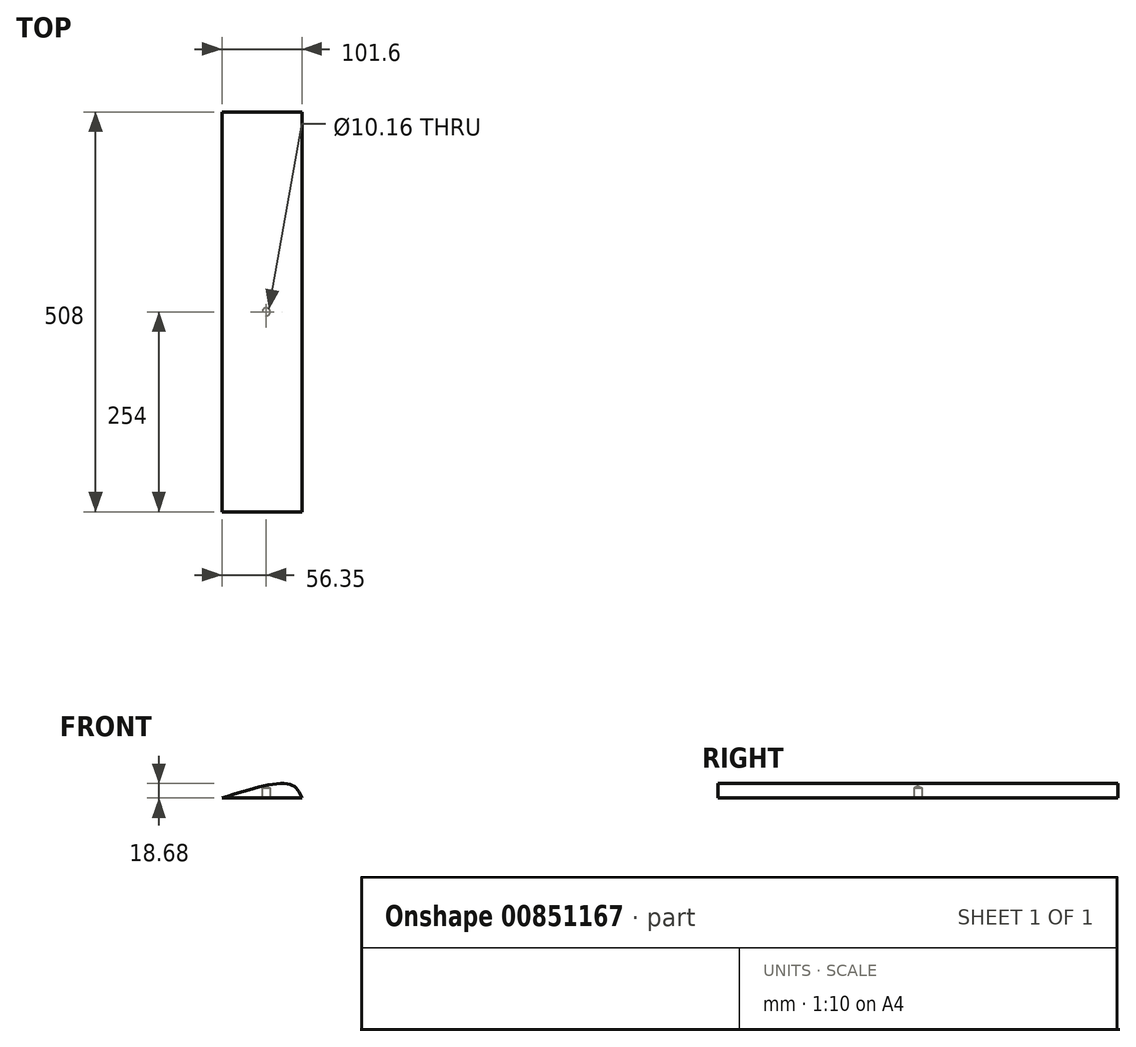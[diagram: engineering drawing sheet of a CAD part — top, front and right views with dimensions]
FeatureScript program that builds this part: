
annotation { "Feature Type Name" : "Feature", "Feature Type Description" : "" }
export const myFeature = defineFeature(function(context is Context, id is Id, definition is map)
    precondition{}
    {
        {
            var Q0;
            Q0=qCreatedBy(makeId("Front.planeOp"),FACE);
            var sketch = newSketch(context, id + "F0", { "sketchPlane" : qUnion([Q0])});
            skLineSegment(sketch, "E0", {"start": v(-56.35, 0) * mm, "end": v(45.25, 0) * mm});
            skFitSpline(sketch, "E1", {"points": [v(45.25, 0) * mm, v(31.12, 17.16) * mm, v(-56.35, 0) * mm], "startDerivative": vector(-27.65, 64.38) * mm, "endDerivative": vector(-160.74, -51.48) * mm});
            skSolve(sketch);
        }
        {
            var Q0;
            Q0=makeQuery(id+"F0.imprint","IMPRINT",FACE,{"disambiguationData":[TD([[makeQuery(id+"F0.imprint","IMPRINT",EDGE,{"derivedFrom":sQuery(id+"F0.wireOp",EDGE,"E0")}),1.0]])]});
            extrude(context, id + "F1", {"entities" : qUnion([Q0]), "endBound" : BoundingType.SYMMETRIC, "depth" : 508 * mm, "offsetDistance" : 25.4 * mm});
        }
        {
            var Q0;
            Q0=makeQuery(id+"F1.opExtrude","SWEPT_FACE",FACE,{"disambiguationData":[OSD([sQuery(id+"F0.wireOp",EDGE,"E0")])]});
            var sketch = newSketch(context, id + "F2", { "sketchPlane" : qUnion([Q0])});
            skCircle(sketch, "E2", {"center": v(0, 0) * mm, "radius": 5.08 * mm});
            skSolve(sketch);
        }
        {
            var Q0;
            Q0=sQuery(id+"F2.wireOp",VERTEX,"E2.center");
            var Q1;
            Q1=makeQuery(id+"F1.opExtrude","SWEPT_BODY",BODY,{"disambiguationData":[OSD([sQuery(id+"F0.wireOp",EDGE,"E0"),sQuery(id+"F0.wireOp",EDGE,"E1")])]});
            hole(context, id + "F3", {"style" : HoleStyle.SIMPLE, "endStyle" : HoleEndStyle.BLIND, "holeDiameter" : 10.16 * mm, "majorDiameter" : 6.35 * mm, "holeDepth" : 12.7 * mm, "isTappedThrough" : true, "tappedDepth" : 12.7 * mm, "tapClearance" : 3, "startFromSketch" : true, "locations" : qUnion([Q0]), "scope" : qUnion([Q1])});
        }
    });
